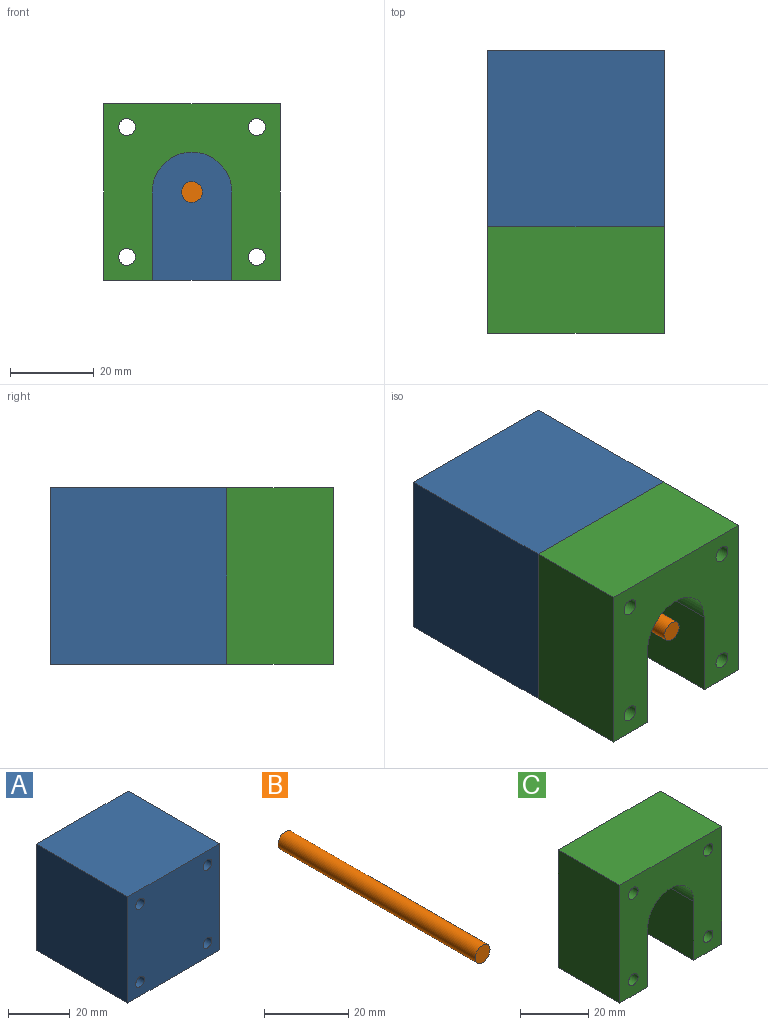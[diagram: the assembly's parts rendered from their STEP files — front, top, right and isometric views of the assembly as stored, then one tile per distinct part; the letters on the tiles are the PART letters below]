
ASSEMBLY  parts=3 mates=2
PART A: 10 faces, bbox 42.2x42x42.2 mm
  f0: plane 42.2x42mm, normal (1,0,0), area 1772.4mm2, adj f1,f7,f8,f9
  f1: plane 42.2x42mm, normal (0,0,1), area 1772.4mm2, adj f0,f2,f8,f9
  f2: plane 42.2x42mm, normal (-1,0,0), area 1772.4mm2, adj f1,f7,f8,f9
  f3: cylinder r=2mm len=42mm, axis (0,1,0), area 527.8mm2, adj f8,f9
  f4: cylinder r=2mm len=42mm, axis (0,1,0), area 527.8mm2, adj f8,f9
  f5: cylinder r=2mm len=42mm, axis (0,1,0), area 527.8mm2, adj f8,f9
  f6: cylinder r=2mm len=42mm, axis (0,1,0), area 527.8mm2, adj f8,f9
  f7: plane 42.2x42mm, normal (0,0,-1), area 1772.4mm2, adj f0,f2,f8,f9
  f8: plane 42.2x42.2mm, normal (0,-1,0), area 1730.6mm2, adj f0,f1,f2,f3,f4,f5,f6,f7
  f9: plane 42.2x42.2mm, normal (0,1,0), area 1730.6mm2, adj f0,f1,f2,f3,f4,f5,f6,f7
PART B: 3 faces, bbox 5x66x5 mm
  f0: cylinder r=2.5mm len=66mm, axis (0,1,0), area 1036.7mm2, adj f1,f2
  f1: plane 5x5mm, normal (0,-1,0), area 19.6mm2, adj f0
  f2: plane 5x5mm, normal (0,1,0), area 19.6mm2, adj f0
PART C: 14 faces, bbox 42.2x25.4x42.2 mm
  f0: cylinder r=9.53mm len=25.4mm, axis (0,1,0), area 760.1mm2, adj f1,f11,f12,f13
  f1: plane 25.4x21.1mm, normal (-1,0,0), area 535.9mm2, adj f0,f2,f12,f13
  f2: plane 25.4x11.58mm, normal (0,0,-1), area 294mm2, adj f1,f3,f12,f13
  f3: plane 42.2x25.4mm, normal (1,0,0), area 1071.9mm2, adj f2,f4,f12,f13
  f4: plane 42.2x25.4mm, normal (0,0,1), area 1071.9mm2, adj f3,f5,f12,f13
  f5: plane 42.2x25.4mm, normal (-1,0,0), area 1071.9mm2, adj f4,f6,f12,f13
  f6: plane 25.4x11.58mm, normal (0,0,-1), area 294mm2, adj f5,f11,f12,f13
  f7: cylinder r=2mm len=25.4mm, axis (0,1,0), area 319.2mm2, adj f12,f13
  f8: cylinder r=2mm len=25.4mm, axis (0,1,0), area 319.2mm2, adj f12,f13
  f9: cylinder r=2mm len=25.4mm, axis (0,1,0), area 319.2mm2, adj f12,f13
  f10: cylinder r=2mm len=25.4mm, axis (0,1,0), area 319.2mm2, adj f12,f13
  f11: plane 25.4x21.1mm, normal (1,0,0), area 535.9mm2, adj f0,f6,f12,f13
  f12: plane 42.2x42.2mm, normal (0,-1,0), area 1186.1mm2, adj f0,f1,f2,f3,f4,f5,f6,f7
  f13: plane 42.2x42.2mm, normal (0,1,0), area 1186.1mm2, adj f0,f1,f2,f3,f4,f5,f6,f7
PLACE A t=(-28.78,8.24,-12.21)mm fixed
PLACE B t=(-28.78,8.24,-12.21)mm
PLACE C t=(-28.78,8.24,-12.21)mm
MATE fastened C.f7 <-> A.f3  axis (0,1,0) through (-44.28,-33.76,3.29)mm
MATE revolute B.f0 <-> A.f9  axis (0,1,0) through (-28.78,8.24,-12.21)mm
